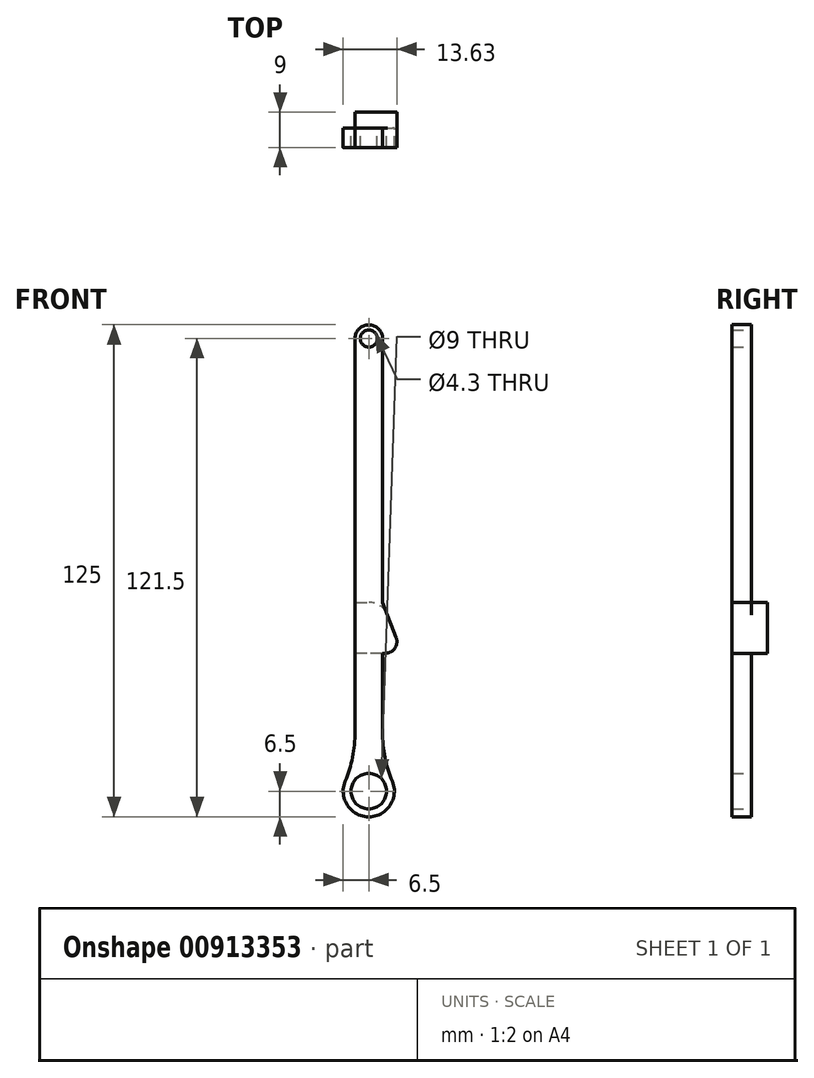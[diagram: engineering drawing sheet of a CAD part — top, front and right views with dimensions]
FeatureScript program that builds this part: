
annotation { "Feature Type Name" : "Feature", "Feature Type Description" : "" }
export const myFeature = defineFeature(function(context is Context, id is Id, definition is map)
    precondition{}
    {
        {
            var Q0;
            Q0=qCreatedBy(makeId("Front.planeOp"),FACE);
            var sketch = newSketch(context, id + "F0", { "sketchPlane" : qUnion([Q0])});
            skCircle(sketch, "E0", {"center": v(0, 0) * mm, "radius": 4.5 * mm});
            skArc(sketch, "E1", {"start": v(-6, 2.5) * mm, "mid": v(0, -6.5) * mm, "end": v(6, 2.5) * mm});
            skArc(sketch, "E2", {"start": v(3.5, 115) * mm, "mid": v(0, 118.5) * mm, "end": v(-3.5, 115) * mm});
            skLineSegment(sketch, "E3", {"start": v(-13.04, 115) * mm, "end": v(14.43, 115) * mm, "construction": true});
            skLineSegment(sketch, "E4", {"start": v(-3.5, 115) * mm, "end": v(-3.5, 15) * mm});
            skLineSegment(sketch, "E5", {"start": v(3.5, 115) * mm, "end": v(3.5, 15) * mm});
            skLineSegment(sketch, "E6", {"start": v(0, 0) * mm, "end": v(-6, 2.5) * mm, "construction": true});
            skArc(sketch, "E7", {"start": v(-6, 2.5) * mm, "mid": v(-4.13, 8.63) * mm, "end": v(-3.5, 15) * mm});
            skArc(sketch, "E8.MirrorCS", {"start": v(6, 2.5) * mm, "mid": v(4.13, 8.63) * mm, "end": v(3.5, 15) * mm});
            skCircle(sketch, "E9", {"center": v(0, 115) * mm, "radius": 2.15 * mm});
            skSolve(sketch);
        }
        {
            var Q0;
            Q0 = qSketchRegion(id + "F0", true);
            extrude(context, id + "F1", {"entities" : qUnion([Q0]), "depth" : 5 * mm, "offsetDistance" : 25.4 * mm, "symmetric" : true});
        }
        {
            var Q0;
            Q0=makeQuery(id+"F1.opExtrude","CAP_FACE",FACE,{"disambiguationData":[OSD([sQuery(id+"F0.wireOp",EDGE,"E0"),sQuery(id+"F0.wireOp",EDGE,"E1"),sQuery(id+"F0.wireOp",EDGE,"E2"),sQuery(id+"F0.wireOp",EDGE,"E4"),sQuery(id+"F0.wireOp",EDGE,"E5"),sQuery(id+"F0.wireOp",EDGE,"E7"),sQuery(id+"F0.wireOp",EDGE,"E8.MirrorCS"),sQuery(id+"F0.wireOp",EDGE,"E9")])],"isStart":false});
            var sketch = newSketch(context, id + "F2", { "sketchPlane" : qUnion([Q0])});
            skLineSegment(sketch, "E10", {"start": v(-3.5, 48) * mm, "end": v(3.5, 48) * mm});
            skLineSegment(sketch, "E11", {"start": v(3.5, 35) * mm, "end": v(-3.5, 35) * mm});
            skLineSegment(sketch, "E12", {"start": v(3.5, 48) * mm, "end": v(8.5, 35) * mm});
            skLineSegment(sketch, "E13", {"start": v(8.5, 35) * mm, "end": v(3.5, 35) * mm});
            skLineSegment(sketch, "E14", {"start": v(-3.5, 35) * mm, "end": v(-3.5, 48) * mm});
            skSolve(sketch);
        }
        {
            var Q0;
            Q0 = qSketchRegion(id + "F2", true);
            extrude(context, id + "F3", {"entities" : qUnion([Q0]), "operationType" : NewBodyOperationType.ADD, "depth" : 0 * mm, "offsetDistance" : 25 * mm, "hasSecondDirection" : true, "secondDirectionOppositeDirection" : true, "secondDirectionDepth" : 9 * mm});
        }
        {
            var Q0;
            {var subQ0=sQuery(id+"F2.wireOp",EDGE,"E10");var subQ1=sQuery(id+"F2.wireOp",EDGE,"E12");Q0=makeQuery(id+"F3.boolean.opBoolean","SPLIT",EDGE,{"disambiguationData":[topologyDisambiguationEdgeConnected([makeQuery(id+"F3.opExtrude","SWEPT_FACE",FACE,{"disambiguationData":[OSD([subQ0])]})])],"derivedFrom":makeQuery(id+"F3.opExtrude","SWEPT_EDGE",EDGE,{"disambiguationData":[OSD([sQuery(id+"F0.wireOp",EDGE,"E5"),subQ0,subQ1])]})});}
            fillet(context, id + "F4", {"entities" : qUnion([Q0]), "radius" : 5 * mm, "tangentPropagation" : true, "allowEdgeOverflow" : false});
        }
        {
            var Q0;
            Q0=makeQuery(id+"F3.opExtrude","SWEPT_EDGE",EDGE,{"disambiguationData":[OSD([sQuery(id+"F2.wireOp",EDGE,"E12"),sQuery(id+"F2.wireOp",EDGE,"E13")])]});
            fillet(context, id + "F5", {"entities" : qUnion([Q0]), "radius" : 3 * mm, "tangentPropagation" : true, "allowEdgeOverflow" : false});
        }
    });
